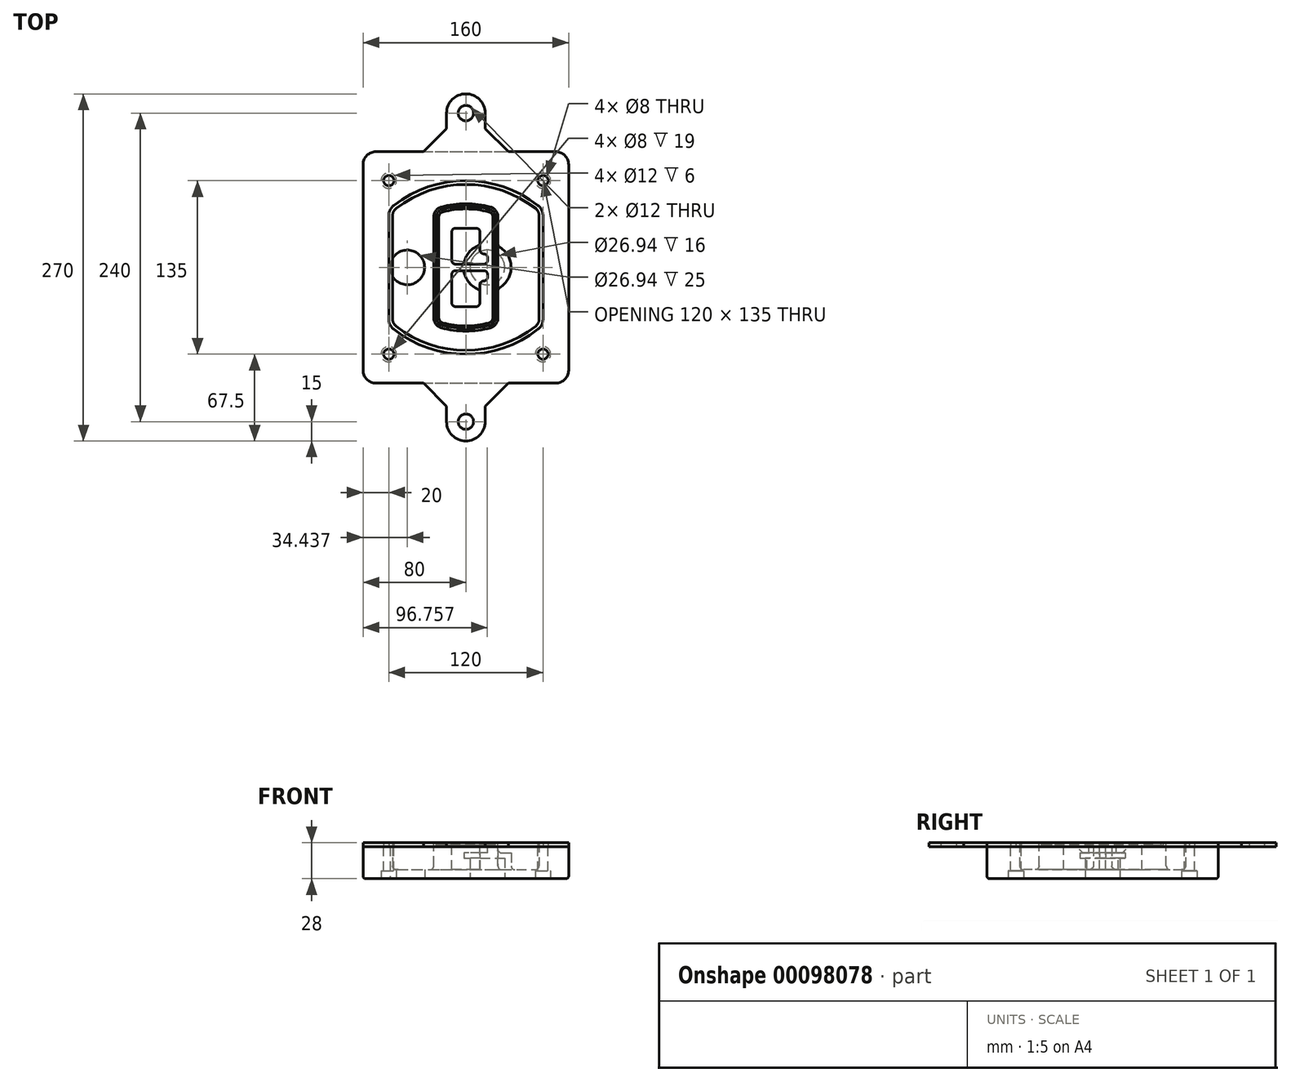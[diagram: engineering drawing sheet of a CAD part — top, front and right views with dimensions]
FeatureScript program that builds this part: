
annotation { "Feature Type Name" : "Feature", "Feature Type Description" : "" }
export const myFeature = defineFeature(function(context is Context, id is Id, definition is map)
    precondition{}
    {
        {
            var Q0;
            Q0=qCreatedBy(makeId("Top.planeOp"),FACE);
            var sketch = newSketch(context, id + "F0", { "sketchPlane" : qUnion([Q0])});
            skPoint(sketch, "E0.rect.middle", {"position": v(0, 0) * mm});
            skLineSegment(sketch, "E1.bottom", {"start": v(-70, -90) * mm, "end": v(70, -90) * mm});
            skLineSegment(sketch, "E1.top", {"start": v(-70, 90) * mm, "end": v(70, 90) * mm});
            skLineSegment(sketch, "E1.left", {"start": v(-80, -80) * mm, "end": v(-80, 80) * mm});
            skLineSegment(sketch, "E1.right", {"start": v(80, -80) * mm, "end": v(80, 80) * mm});
            skLineSegment(sketch, "E2", {"start": v(-80, 90) * mm, "end": v(80, -90) * mm, "construction": true});
            skLineSegment(sketch, "E3", {"start": v(80, 90) * mm, "end": v(-80, -90) * mm, "construction": true});
            skCircle(sketch, "E4", {"center": v(-60, 67.5) * mm, "radius": 4 * mm});
            skCircle(sketch, "E5", {"center": v(60, 67.5) * mm, "radius": 4 * mm});
            skCircle(sketch, "E6", {"center": v(60, -67.5) * mm, "radius": 4 * mm});
            skCircle(sketch, "E7", {"center": v(-60, -67.5) * mm, "radius": 4 * mm});
            skLineSegment(sketch, "E8", {"start": v(-60, 67.5) * mm, "end": v(60, 67.5) * mm, "construction": true});
            skLineSegment(sketch, "E9", {"start": v(60, 67.5) * mm, "end": v(60, -67.5) * mm, "construction": true});
            skLineSegment(sketch, "E10", {"start": v(60, -67.5) * mm, "end": v(-60, -67.5) * mm, "construction": true});
            skLineSegment(sketch, "E11", {"start": v(-60, -67.5) * mm, "end": v(-60, 67.5) * mm, "construction": true});
            skLineSegment(sketch, "E12", {"start": v(-60, 40.3) * mm, "end": v(-60, -40.3) * mm});
            skLineSegment(sketch, "E13", {"start": v(60, 40.3) * mm, "end": v(60, -40.3) * mm});
            skArc(sketch, "E14", {"start": v(56.15, 48.18) * mm, "mid": v(0, 67.5) * mm, "end": v(-56.15, 48.18) * mm});
            skArc(sketch, "E15", {"start": v(-56.15, -48.18) * mm, "mid": v(0, -67.5) * mm, "end": v(56.15, -48.18) * mm});
            skLineSegment(sketch, "E16", {"start": v(-60, 0) * mm, "end": v(60, 0) * mm, "construction": true});
            skPoint(sketch, "E17.visualSharp", {"position": v(-60, -45) * mm});
            skArc(sketch, "E17.filletArc", {"start": v(-60, -40.3) * mm, "mid": v(-58.99, -44.68) * mm, "end": v(-56.15, -48.18) * mm});
            skPoint(sketch, "E18.visualSharp", {"position": v(-60, 45) * mm});
            skArc(sketch, "E18.filletArc", {"start": v(-56.15, 48.18) * mm, "mid": v(-58.99, 44.68) * mm, "end": v(-60, 40.3) * mm});
            skPoint(sketch, "E19.visualSharp", {"position": v(60, 45) * mm});
            skArc(sketch, "E19.filletArc", {"start": v(60, 40.3) * mm, "mid": v(58.99, 44.68) * mm, "end": v(56.15, 48.18) * mm});
            skPoint(sketch, "E20.visualSharp", {"position": v(60, -45) * mm});
            skArc(sketch, "E20.filletArc", {"start": v(56.15, -48.18) * mm, "mid": v(58.99, -44.68) * mm, "end": v(60, -40.3) * mm});
            skPoint(sketch, "E21.visualSharp", {"position": v(-80, 90) * mm});
            skArc(sketch, "E21.filletArc", {"start": v(-70, 90) * mm, "mid": v(-77.07, 87.07) * mm, "end": v(-80, 80) * mm});
            skPoint(sketch, "E22.visualSharp", {"position": v(80, 90) * mm});
            skArc(sketch, "E22.filletArc", {"start": v(80, 80) * mm, "mid": v(77.07, 87.07) * mm, "end": v(70, 90) * mm});
            skPoint(sketch, "E23.visualSharp", {"position": v(80, -90) * mm});
            skArc(sketch, "E23.filletArc", {"start": v(70, -90) * mm, "mid": v(77.07, -87.07) * mm, "end": v(80, -80) * mm});
            skPoint(sketch, "E24.visualSharp", {"position": v(-80, -90) * mm});
            skArc(sketch, "E24.filletArc", {"start": v(-80, -80) * mm, "mid": v(-77.07, -87.07) * mm, "end": v(-70, -90) * mm});
            skArc(sketch, "E25.0", {"start": v(57, 40.3) * mm, "mid": v(56.3, 43.36) * mm, "end": v(54.3, 45.81) * mm});
            skLineSegment(sketch, "E25.1", {"start": v(57, 40.3) * mm, "end": v(57, -40.3) * mm});
            skArc(sketch, "E25.2", {"start": v(54.3, -45.81) * mm, "mid": v(56.3, -43.36) * mm, "end": v(57, -40.3) * mm});
            skArc(sketch, "E25.3", {"start": v(-54.3, -45.81) * mm, "mid": v(0, -64.5) * mm, "end": v(54.3, -45.81) * mm});
            skArc(sketch, "E25.4", {"start": v(-57, -40.3) * mm, "mid": v(-56.3, -43.36) * mm, "end": v(-54.3, -45.81) * mm});
            skArc(sketch, "E25.5", {"start": v(54.3, 45.81) * mm, "mid": v(0, 64.5) * mm, "end": v(-54.3, 45.81) * mm});
            skLineSegment(sketch, "E25.6", {"start": v(-57, 40.3) * mm, "end": v(-57, -40.3) * mm});
            skArc(sketch, "E25.7", {"start": v(-54.3, 45.81) * mm, "mid": v(-56.3, 43.36) * mm, "end": v(-57, 40.3) * mm});
            skArc(sketch, "E26.0", {"start": v(-58.62, 51.33) * mm, "mid": v(-62.58, 46.43) * mm, "end": v(-64, 40.3) * mm});
            skArc(sketch, "E26.1", {"start": v(58.62, 51.33) * mm, "mid": v(0, 71.5) * mm, "end": v(-58.62, 51.33) * mm});
            skArc(sketch, "E26.2", {"start": v(64, 40.3) * mm, "mid": v(62.58, 46.43) * mm, "end": v(58.62, 51.33) * mm});
            skLineSegment(sketch, "E26.3", {"start": v(64, 40.3) * mm, "end": v(64, -40.3) * mm});
            skArc(sketch, "E26.4", {"start": v(58.62, -51.33) * mm, "mid": v(62.58, -46.43) * mm, "end": v(64, -40.3) * mm});
            skLineSegment(sketch, "E26.5", {"start": v(-64, 40.3) * mm, "end": v(-64, -40.3) * mm});
            skArc(sketch, "E26.6", {"start": v(-58.62, -51.33) * mm, "mid": v(0, -71.5) * mm, "end": v(58.62, -51.33) * mm});
            skArc(sketch, "E26.7", {"start": v(-64, -40.3) * mm, "mid": v(-62.58, -46.43) * mm, "end": v(-58.62, -51.33) * mm});
            skSolve(sketch);
        }
        {
            var Q0;
            Q0=makeQuery(id+"F0.imprint","IMPRINT",FACE,{"disambiguationData":[TD([[makeQuery(id+"F0.imprint","IMPRINT",EDGE,{"derivedFrom":sQuery(id+"F0.wireOp",EDGE,"E1.bottom")}),1.0]])]});
            var Q1;
            Q1=makeQuery(id+"F0.imprint","IMPRINT",FACE,{"disambiguationData":[TD([[makeQuery(id+"F0.imprint","IMPRINT",EDGE,{"derivedFrom":sQuery(id+"F0.wireOp",EDGE,"E12")}),1.0]])]});
            var Q2;
            Q2=makeQuery(id+"F0.imprint","IMPRINT",FACE,{"disambiguationData":[TD([[makeQuery(id+"F0.imprint","IMPRINT",EDGE,{"derivedFrom":sQuery(id+"F0.wireOp",EDGE,"E25.0")}),1.0]])]});
            var Q3;
            Q3=makeQuery(id+"F0.imprint","IMPRINT",FACE,{"disambiguationData":[TD([[makeQuery(id+"F0.imprint","IMPRINT",EDGE,{"derivedFrom":sQuery(id+"F0.wireOp",EDGE,"E12")}),-1.0]])]});
            extrude(context, id + "F1", {"entities" : qUnion([Q0, Q1, Q2, Q3]), "oppositeDirection" : true, "depth" : 25 * mm});
        }
        {
            var Q0;
            Q0=makeQuery(id+"F0.imprint","IMPRINT",FACE,{"disambiguationData":[TD([[makeQuery(id+"F0.imprint","IMPRINT",EDGE,{"derivedFrom":sQuery(id+"F0.wireOp",EDGE,"E12")}),1.0]])]});
            extrude(context, id + "F2", {"entities" : qUnion([Q0]), "operationType" : NewBodyOperationType.ADD, "depth" : 3 * mm});
        }
        {
            var Q0;
            Q0=makeQuery(id+"F0.imprint","IMPRINT",FACE,{"disambiguationData":[TD([[makeQuery(id+"F0.imprint","IMPRINT",EDGE,{"derivedFrom":sQuery(id+"F0.wireOp",EDGE,"E25.0")}),1.0]])]});
            extrude(context, id + "F3", {"entities" : qUnion([Q0]), "operationType" : NewBodyOperationType.REMOVE, "oppositeDirection" : true, "depth" : 18 * mm});
        }
        {
            var Q0;
            Q0=makeQuery(id+"F2.opExtrude","CAP_FACE",FACE,{"disambiguationData":[OSD([sQuery(id+"F0.wireOp",EDGE,"E12"),sQuery(id+"F0.wireOp",EDGE,"E13"),sQuery(id+"F0.wireOp",EDGE,"E14"),sQuery(id+"F0.wireOp",EDGE,"E15"),sQuery(id+"F0.wireOp",EDGE,"E17.filletArc"),sQuery(id+"F0.wireOp",EDGE,"E18.filletArc"),sQuery(id+"F0.wireOp",EDGE,"E19.filletArc"),sQuery(id+"F0.wireOp",EDGE,"E20.filletArc"),sQuery(id+"F0.wireOp",EDGE,"E25.0"),sQuery(id+"F0.wireOp",EDGE,"E25.1"),sQuery(id+"F0.wireOp",EDGE,"E25.2"),sQuery(id+"F0.wireOp",EDGE,"E25.3"),sQuery(id+"F0.wireOp",EDGE,"E25.4"),sQuery(id+"F0.wireOp",EDGE,"E25.5"),sQuery(id+"F0.wireOp",EDGE,"E25.6"),sQuery(id+"F0.wireOp",EDGE,"E25.7")])],"isStart":false});
            var sketch = newSketch(context, id + "F4", { "sketchPlane" : qUnion([Q0])});
            skArc(sketch, "E27.0", {"start": v(-19.08, -46.97) * mm, "mid": v(0, -49.5) * mm, "end": v(19.08, -46.97) * mm});
            skArc(sketch, "E28.0", {"start": v(19.08, 46.97) * mm, "mid": v(0, 49.5) * mm, "end": v(-19.08, 46.97) * mm});
            skLineSegment(sketch, "E29", {"start": v(-25, 39.25) * mm, "end": v(-25, -39.25) * mm});
            skLineSegment(sketch, "E30", {"start": v(25, 39.25) * mm, "end": v(25, -39.25) * mm});
            skLineSegment(sketch, "E31", {"start": v(-25, 45.1) * mm, "end": v(25, 45.1) * mm, "construction": true});
            skLineSegment(sketch, "E32", {"start": v(-25, -45.1) * mm, "end": v(25, -45.1) * mm, "construction": true});
            skPoint(sketch, "E33.visualSharp", {"position": v(-25, 45.1) * mm});
            skArc(sketch, "E33.filletArc", {"start": v(-19.08, 46.97) * mm, "mid": v(-23.35, 44.11) * mm, "end": v(-25, 39.25) * mm});
            skPoint(sketch, "E34.visualSharp", {"position": v(25, 45.1) * mm});
            skArc(sketch, "E34.filletArc", {"start": v(25, 39.25) * mm, "mid": v(23.35, 44.11) * mm, "end": v(19.08, 46.97) * mm});
            skPoint(sketch, "E35.visualSharp", {"position": v(25, -45.1) * mm});
            skArc(sketch, "E35.filletArc", {"start": v(19.08, -46.97) * mm, "mid": v(23.35, -44.11) * mm, "end": v(25, -39.25) * mm});
            skPoint(sketch, "E36.visualSharp", {"position": v(-25, -45.1) * mm});
            skArc(sketch, "E36.filletArc", {"start": v(-25, -39.25) * mm, "mid": v(-23.35, -44.11) * mm, "end": v(-19.08, -46.97) * mm});
            skArc(sketch, "E37.0", {"start": v(54.3, 45.81) * mm, "mid": v(0, 64.5) * mm, "end": v(-54.3, 45.81) * mm});
            skArc(sketch, "E37.1", {"start": v(-54.3, 45.81) * mm, "mid": v(-56.3, 43.36) * mm, "end": v(-57, 40.3) * mm});
            skLineSegment(sketch, "E37.2", {"start": v(-57, 40.3) * mm, "end": v(-57, -40.3) * mm});
            skArc(sketch, "E37.3", {"start": v(-57, -40.3) * mm, "mid": v(-56.3, -43.36) * mm, "end": v(-54.3, -45.81) * mm});
            skArc(sketch, "E37.4", {"start": v(-54.3, -45.81) * mm, "mid": v(0, -64.5) * mm, "end": v(54.3, -45.81) * mm});
            skArc(sketch, "E37.5", {"start": v(54.3, -45.81) * mm, "mid": v(56.3, -43.36) * mm, "end": v(57, -40.3) * mm});
            skLineSegment(sketch, "E37.6", {"start": v(57, 40.3) * mm, "end": v(57, -40.3) * mm});
            skArc(sketch, "E37.7", {"start": v(57, 40.3) * mm, "mid": v(56.3, 43.36) * mm, "end": v(54.3, 45.81) * mm});
            skLineSegment(sketch, "E38.0", {"start": v(23, 39.25) * mm, "end": v(23, -39.25) * mm});
            skArc(sketch, "E38.1", {"start": v(18.56, -45.04) * mm, "mid": v(21.76, -42.9) * mm, "end": v(23, -39.25) * mm});
            skArc(sketch, "E38.2", {"start": v(-18.56, -45.04) * mm, "mid": v(0, -47.5) * mm, "end": v(18.56, -45.04) * mm});
            skArc(sketch, "E38.3", {"start": v(-23, -39.25) * mm, "mid": v(-21.76, -42.9) * mm, "end": v(-18.56, -45.04) * mm});
            skLineSegment(sketch, "E38.4", {"start": v(-23, 39.25) * mm, "end": v(-23, -39.25) * mm});
            skArc(sketch, "E38.5", {"start": v(23, 39.25) * mm, "mid": v(21.76, 42.9) * mm, "end": v(18.56, 45.04) * mm});
            skArc(sketch, "E38.6", {"start": v(-18.56, 45.04) * mm, "mid": v(-21.76, 42.9) * mm, "end": v(-23, 39.25) * mm});
            skArc(sketch, "E38.7", {"start": v(18.56, 45.04) * mm, "mid": v(0, 47.5) * mm, "end": v(-18.56, 45.04) * mm});
            skArc(sketch, "E39.0", {"start": v(21, 39.25) * mm, "mid": v(20.18, 41.68) * mm, "end": v(18.04, 43.1) * mm});
            skLineSegment(sketch, "E39.1", {"start": v(21, 39.25) * mm, "end": v(21, -39.25) * mm});
            skArc(sketch, "E39.2", {"start": v(18.04, -43.1) * mm, "mid": v(20.18, -41.68) * mm, "end": v(21, -39.25) * mm});
            skArc(sketch, "E39.3", {"start": v(-18.04, -43.1) * mm, "mid": v(0, -45.5) * mm, "end": v(18.04, -43.1) * mm});
            skArc(sketch, "E39.4", {"start": v(-21, -39.25) * mm, "mid": v(-20.18, -41.68) * mm, "end": v(-18.04, -43.1) * mm});
            skArc(sketch, "E39.5", {"start": v(18.04, 43.1) * mm, "mid": v(0, 45.5) * mm, "end": v(-18.04, 43.1) * mm});
            skLineSegment(sketch, "E39.6", {"start": v(-21, 39.25) * mm, "end": v(-21, -39.25) * mm});
            skArc(sketch, "E39.7", {"start": v(-18.04, 43.1) * mm, "mid": v(-20.18, 41.68) * mm, "end": v(-21, 39.25) * mm});
            skLineSegment(sketch, "E40", {"start": v(-25, 0) * mm, "end": v(25, 0) * mm, "construction": true});
            skLineSegment(sketch, "E41", {"start": v(-11, 5.5) * mm, "end": v(-11, 27.5) * mm});
            skLineSegment(sketch, "E42", {"start": v(-8, 30.5) * mm, "end": v(8, 30.5) * mm});
            skLineSegment(sketch, "E43", {"start": v(11, 27.5) * mm, "end": v(11, 13.5) * mm});
            skLineSegment(sketch, "E44", {"start": v(14, 10.5) * mm, "end": v(14, 10.5) * mm});
            skLineSegment(sketch, "E45", {"start": v(17, 7.5) * mm, "end": v(17, 5.5) * mm});
            skLineSegment(sketch, "E46", {"start": v(14, 2.5) * mm, "end": v(-8, 2.5) * mm});
            skPoint(sketch, "E47.visualSharp", {"position": v(-11, 30.5) * mm});
            skArc(sketch, "E47.filletArc", {"start": v(-8, 30.5) * mm, "mid": v(-10.12, 29.62) * mm, "end": v(-11, 27.5) * mm});
            skPoint(sketch, "E48.visualSharp", {"position": v(11, 30.5) * mm});
            skArc(sketch, "E48.filletArc", {"start": v(11, 27.5) * mm, "mid": v(10.12, 29.62) * mm, "end": v(8, 30.5) * mm});
            skPoint(sketch, "E49.visualSharp", {"position": v(11, 10.5) * mm});
            skArc(sketch, "E49.filletArc", {"start": v(11, 13.5) * mm, "mid": v(11.88, 11.38) * mm, "end": v(14, 10.5) * mm});
            skPoint(sketch, "E50.visualSharp", {"position": v(17, 10.5) * mm});
            skArc(sketch, "E50.filletArc", {"start": v(17, 7.5) * mm, "mid": v(16.12, 9.62) * mm, "end": v(14, 10.5) * mm});
            skPoint(sketch, "E51.visualSharp", {"position": v(17, 2.5) * mm});
            skArc(sketch, "E51.filletArc", {"start": v(14, 2.5) * mm, "mid": v(16.12, 3.38) * mm, "end": v(17, 5.5) * mm});
            skPoint(sketch, "E52.visualSharp", {"position": v(-11, 2.5) * mm});
            skArc(sketch, "E52.filletArc", {"start": v(-11, 5.5) * mm, "mid": v(-10.12, 3.38) * mm, "end": v(-8, 2.5) * mm});
            skLineSegment(sketch, "E53.0.MirrorCS", {"start": v(14, -2.5) * mm, "end": v(-8, -2.5) * mm});
            skArc(sketch, "E54.0.MirrorCS", {"start": v(-11, -5.5) * mm, "mid": v(-10.12, -3.38) * mm, "end": v(-8, -2.5) * mm});
            skLineSegment(sketch, "E55.0.MirrorCS", {"start": v(-11, -5.5) * mm, "end": v(-11, -27.5) * mm});
            skArc(sketch, "E56.0.MirrorCS", {"start": v(-8, -30.5) * mm, "mid": v(-10.12, -29.62) * mm, "end": v(-11, -27.5) * mm});
            skLineSegment(sketch, "E57.0.MirrorCS", {"start": v(-8, -30.5) * mm, "end": v(8, -30.5) * mm});
            skArc(sketch, "E58.0.MirrorCS", {"start": v(11, -27.5) * mm, "mid": v(10.12, -29.62) * mm, "end": v(8, -30.5) * mm});
            skLineSegment(sketch, "E59.0.MirrorCS", {"start": v(11, -27.5) * mm, "end": v(11, -13.5) * mm});
            skArc(sketch, "E60.0.MirrorCS", {"start": v(11, -13.5) * mm, "mid": v(11.88, -11.38) * mm, "end": v(14, -10.5) * mm});
            skArc(sketch, "E61.0.MirrorCS", {"start": v(17, -7.5) * mm, "mid": v(16.12, -9.62) * mm, "end": v(14, -10.5) * mm});
            skLineSegment(sketch, "E62.0.MirrorCS", {"start": v(17, -7.5) * mm, "end": v(17, -5.5) * mm});
            skArc(sketch, "E63.0.MirrorCS", {"start": v(14, -2.5) * mm, "mid": v(16.12, -3.38) * mm, "end": v(17, -5.5) * mm});
            skSolve(sketch);
        }
        {
            var Q0;
            Q0=makeQuery(id+"F4.imprint","IMPRINT",FACE,{"disambiguationData":[TD([[makeQuery(id+"F4.imprint","IMPRINT",EDGE,{"derivedFrom":sQuery(id+"F4.wireOp",EDGE,"E27.0")}),1.0]])]});
            var Q1;
            Q1=makeQuery(id+"F4.imprint","IMPRINT",FACE,{"disambiguationData":[TD([[makeQuery(id+"F4.imprint","IMPRINT",EDGE,{"derivedFrom":sQuery(id+"F4.wireOp",EDGE,"E38.0")}),-1.0]])]});
            var Q2;
            Q2=makeQuery(id+"F4.imprint","IMPRINT",FACE,{"disambiguationData":[TD([[makeQuery(id+"F4.imprint","IMPRINT",EDGE,{"derivedFrom":sQuery(id+"F4.wireOp",EDGE,"E39.0")}),1.0]])]});
            extrude(context, id + "F5", {"entities" : qUnion([Q0, Q1, Q2]), "operationType" : NewBodyOperationType.ADD, "endBound" : BoundingType.UP_TO_NEXT, "oppositeDirection" : true, "depth" : 25 * mm});
        }
        {
            var Q0;
            Q0=makeQuery(id+"F4.imprint","IMPRINT",FACE,{"disambiguationData":[TD([[makeQuery(id+"F4.imprint","IMPRINT",EDGE,{"derivedFrom":sQuery(id+"F4.wireOp",EDGE,"E38.0")}),-1.0]])]});
            extrude(context, id + "F6", {"entities" : qUnion([Q0]), "operationType" : NewBodyOperationType.REMOVE, "oppositeDirection" : true, "depth" : 2 * mm});
        }
        {
            var Q0;
            Q0=makeQuery(id+"F1.opExtrude","CAP_FACE",FACE,{"disambiguationData":[OSD([sQuery(id+"F0.wireOp",EDGE,"E1.bottom"),sQuery(id+"F0.wireOp",EDGE,"E1.top"),sQuery(id+"F0.wireOp",EDGE,"E1.left"),sQuery(id+"F0.wireOp",EDGE,"E1.right"),sQuery(id+"F0.wireOp",EDGE,"E4"),sQuery(id+"F0.wireOp",EDGE,"E5"),sQuery(id+"F0.wireOp",EDGE,"E6"),sQuery(id+"F0.wireOp",EDGE,"E7"),sQuery(id+"F0.wireOp",EDGE,"E21.filletArc"),sQuery(id+"F0.wireOp",EDGE,"E22.filletArc"),sQuery(id+"F0.wireOp",EDGE,"E23.filletArc"),sQuery(id+"F0.wireOp",EDGE,"E24.filletArc")])],"isStart":false});
            var sketch = newSketch(context, id + "F7", { "sketchPlane" : qUnion([Q0])});
            skCircle(sketch, "E64", {"center": v(16.76, 0) * mm, "radius": 13.47 * mm});
            skCircle(sketch, "E65", {"center": v(-45.56, 0) * mm, "radius": 13.47 * mm});
            skLineSegment(sketch, "E66", {"start": v(80, 0) * mm, "end": v(-80, 0) * mm});
            skCircle(sketch, "E67", {"center": v(16.76, 0) * mm, "radius": 18.47 * mm});
            skCircle(sketch, "E68", {"center": v(60, -67.5) * mm, "radius": 6 * mm});
            skCircle(sketch, "E69", {"center": v(-60, -67.5) * mm, "radius": 6 * mm});
            skCircle(sketch, "E70", {"center": v(-60, 67.5) * mm, "radius": 6 * mm});
            skCircle(sketch, "E71", {"center": v(60, 67.5) * mm, "radius": 6 * mm});
            skSolve(sketch);
        }
        {
            var Q0;
            {var subQ1=sQuery(id+"F7.wireOp",EDGE,"E66");var subQ4=sQuery(id+"F7.wireOp",EDGE,"E64");var subQ6=makeQuery(id+"F7.imprint","INTERSECT",VERTEX,{"disambiguationData":[OD(0.0)],"derivedFrom":[subQ4,subQ1]});Q0=makeQuery(id+"F7.imprint","IMPRINT",FACE,{"disambiguationData":[TD([[makeQuery(id+"F7.imprint","IMPRINT",EDGE,{"disambiguationData":[TD([[subQ6,-1.0]])],"derivedFrom":subQ4}),-1.0]])]});}
            var Q1;
            {var subQ0=sQuery(id+"F7.wireOp",EDGE,"E66");var subQ1=sQuery(id+"F7.wireOp",EDGE,"E64");var subQ3=makeQuery(id+"F7.imprint","INTERSECT",VERTEX,{"disambiguationData":[OD(0.0)],"derivedFrom":[subQ1,subQ0]});Q1=makeQuery(id+"F7.imprint","IMPRINT",FACE,{"disambiguationData":[TD([[makeQuery(id+"F7.imprint","IMPRINT",EDGE,{"disambiguationData":[TD([[subQ3,-1.0]])],"derivedFrom":subQ1}),1.0]])]});}
            var Q2;
            {var subQ0=sQuery(id+"F7.wireOp",EDGE,"E66");var subQ1=sQuery(id+"F7.wireOp",EDGE,"E64");var subQ3=makeQuery(id+"F7.imprint","INTERSECT",VERTEX,{"disambiguationData":[OD(0.0)],"derivedFrom":[subQ1,subQ0]});Q2=makeQuery(id+"F7.imprint","IMPRINT",FACE,{"disambiguationData":[TD([[makeQuery(id+"F7.imprint","IMPRINT",EDGE,{"disambiguationData":[TD([[subQ3,1.0]])],"derivedFrom":subQ1}),1.0]])]});}
            var Q3;
            {var subQ1=sQuery(id+"F7.wireOp",EDGE,"E66");var subQ4=sQuery(id+"F7.wireOp",EDGE,"E64");var subQ6=makeQuery(id+"F7.imprint","INTERSECT",VERTEX,{"disambiguationData":[OD(0.0)],"derivedFrom":[subQ4,subQ1]});Q3=makeQuery(id+"F7.imprint","IMPRINT",FACE,{"disambiguationData":[TD([[makeQuery(id+"F7.imprint","IMPRINT",EDGE,{"disambiguationData":[TD([[subQ6,1.0]])],"derivedFrom":subQ4}),-1.0]])]});}
            extrude(context, id + "F8", {"entities" : qUnion([Q0, Q1, Q2, Q3]), "operationType" : NewBodyOperationType.ADD, "oppositeDirection" : true, "depth" : 20 * mm});
        }
        {
            var Q0;
            {var subQ0=sQuery(id+"F7.wireOp",EDGE,"E66");var subQ1=sQuery(id+"F7.wireOp",EDGE,"E64");var subQ3=makeQuery(id+"F7.imprint","INTERSECT",VERTEX,{"disambiguationData":[OD(0.0)],"derivedFrom":[subQ1,subQ0]});Q0=makeQuery(id+"F7.imprint","IMPRINT",FACE,{"disambiguationData":[TD([[makeQuery(id+"F7.imprint","IMPRINT",EDGE,{"disambiguationData":[TD([[subQ3,-1.0]])],"derivedFrom":subQ1}),1.0]])]});}
            var Q1;
            {var subQ0=sQuery(id+"F7.wireOp",EDGE,"E66");var subQ1=sQuery(id+"F7.wireOp",EDGE,"E64");var subQ3=makeQuery(id+"F7.imprint","INTERSECT",VERTEX,{"disambiguationData":[OD(0.0)],"derivedFrom":[subQ1,subQ0]});Q1=makeQuery(id+"F7.imprint","IMPRINT",FACE,{"disambiguationData":[TD([[makeQuery(id+"F7.imprint","IMPRINT",EDGE,{"disambiguationData":[TD([[subQ3,1.0]])],"derivedFrom":subQ1}),1.0]])]});}
            extrude(context, id + "F9", {"entities" : qUnion([Q0, Q1]), "operationType" : NewBodyOperationType.REMOVE, "oppositeDirection" : true, "depth" : 16 * mm});
        }
        {
            var Q0;
            {var subQ0=sQuery(id+"F7.wireOp",EDGE,"E66");var subQ1=sQuery(id+"F7.wireOp",EDGE,"E65");var subQ3=makeQuery(id+"F7.imprint","INTERSECT",VERTEX,{"disambiguationData":[OD(0.0)],"derivedFrom":[subQ1,subQ0]});Q0=makeQuery(id+"F7.imprint","IMPRINT",FACE,{"disambiguationData":[TD([[makeQuery(id+"F7.imprint","IMPRINT",EDGE,{"disambiguationData":[TD([[subQ3,-1.0]])],"derivedFrom":subQ1}),1.0]])]});}
            var Q1;
            {var subQ0=sQuery(id+"F7.wireOp",EDGE,"E66");var subQ1=sQuery(id+"F7.wireOp",EDGE,"E65");var subQ3=makeQuery(id+"F7.imprint","INTERSECT",VERTEX,{"disambiguationData":[OD(0.0)],"derivedFrom":[subQ1,subQ0]});Q1=makeQuery(id+"F7.imprint","IMPRINT",FACE,{"disambiguationData":[TD([[makeQuery(id+"F7.imprint","IMPRINT",EDGE,{"disambiguationData":[TD([[subQ3,1.0]])],"derivedFrom":subQ1}),1.0]])]});}
            extrude(context, id + "F10", {"entities" : qUnion([Q0, Q1]), "operationType" : NewBodyOperationType.REMOVE, "oppositeDirection" : true, "depth" : 25 * mm});
        }
        {
            var Q0;
            Q0=makeQuery(id+"F7.imprint","IMPRINT",FACE,{"disambiguationData":[TD([[makeQuery(id+"F7.imprint","IMPRINT",EDGE,{"derivedFrom":sQuery(id+"F7.wireOp",EDGE,"E68")}),1.0]])]});
            var Q1;
            Q1=makeQuery(id+"F7.imprint","IMPRINT",FACE,{"disambiguationData":[TD([[makeQuery(id+"F7.imprint","IMPRINT",EDGE,{"derivedFrom":makeQuery(id+"F1.opExtrude","CAP_EDGE",EDGE,{"disambiguationData":[OSD([sQuery(id+"F0.wireOp",EDGE,"E5")])],"isStart":false})}),-1.0]])]});
            var Q2;
            Q2=makeQuery(id+"F7.imprint","IMPRINT",FACE,{"disambiguationData":[TD([[makeQuery(id+"F7.imprint","IMPRINT",EDGE,{"derivedFrom":sQuery(id+"F7.wireOp",EDGE,"E69")}),1.0]])]});
            var Q3;
            Q3=makeQuery(id+"F7.imprint","IMPRINT",FACE,{"disambiguationData":[TD([[makeQuery(id+"F7.imprint","IMPRINT",EDGE,{"derivedFrom":makeQuery(id+"F1.opExtrude","CAP_EDGE",EDGE,{"disambiguationData":[OSD([sQuery(id+"F0.wireOp",EDGE,"E4")])],"isStart":false})}),-1.0]])]});
            var Q4;
            Q4=makeQuery(id+"F7.imprint","IMPRINT",FACE,{"disambiguationData":[TD([[makeQuery(id+"F7.imprint","IMPRINT",EDGE,{"derivedFrom":sQuery(id+"F7.wireOp",EDGE,"E70")}),1.0]])]});
            var Q5;
            Q5=makeQuery(id+"F7.imprint","IMPRINT",FACE,{"disambiguationData":[TD([[makeQuery(id+"F7.imprint","IMPRINT",EDGE,{"derivedFrom":makeQuery(id+"F1.opExtrude","CAP_EDGE",EDGE,{"disambiguationData":[OSD([sQuery(id+"F0.wireOp",EDGE,"E7")])],"isStart":false})}),-1.0]])]});
            var Q6;
            Q6=makeQuery(id+"F7.imprint","IMPRINT",FACE,{"disambiguationData":[TD([[makeQuery(id+"F7.imprint","IMPRINT",EDGE,{"derivedFrom":sQuery(id+"F7.wireOp",EDGE,"E71")}),1.0]])]});
            var Q7;
            Q7=makeQuery(id+"F7.imprint","IMPRINT",FACE,{"disambiguationData":[TD([[makeQuery(id+"F7.imprint","IMPRINT",EDGE,{"derivedFrom":makeQuery(id+"F1.opExtrude","CAP_EDGE",EDGE,{"disambiguationData":[OSD([sQuery(id+"F0.wireOp",EDGE,"E6")])],"isStart":false})}),-1.0]])]});
            extrude(context, id + "F11", {"entities" : qUnion([Q0, Q1, Q2, Q3, Q4, Q5, Q6, Q7]), "operationType" : NewBodyOperationType.REMOVE, "oppositeDirection" : true, "depth" : 6 * mm});
        }
        {
            var Q0;
            Q0=makeQuery(id+"F9.boolean.opBoolean","COPY",FACE,{"derivedFrom":makeQuery(id+"F9.opExtrude","CAP_FACE",FACE,{"disambiguationData":[OSD([sQuery(id+"F7.wireOp",EDGE,"E64")])],"isStart":false})});
            var sketch = newSketch(context, id + "F12", { "sketchPlane" : qUnion([Q0])});
            skArc(sketch, "E72.0", {"start": v(11, 17.55) * mm, "mid": v(2.57, 11.82) * mm, "end": v(-1.54, 2.5) * mm});
            skArc(sketch, "E72.1", {"start": v(-1.54, -2.5) * mm, "mid": v(2.57, -11.82) * mm, "end": v(11, -17.55) * mm});
            skLineSegment(sketch, "E73", {"start": v(-1.54, -2.5) * mm, "end": v(14, -2.5) * mm});
            skLineSegment(sketch, "E74.0", {"start": v(14, 2.5) * mm, "end": v(-1.54, 2.5) * mm});
            skArc(sketch, "E74.1", {"start": v(14, 2.5) * mm, "mid": v(16.12, 3.38) * mm, "end": v(17, 5.5) * mm});
            skLineSegment(sketch, "E74.2", {"start": v(17, 7.5) * mm, "end": v(17, 5.5) * mm});
            skArc(sketch, "E74.3", {"start": v(17, 7.5) * mm, "mid": v(16.12, 9.62) * mm, "end": v(14, 10.5) * mm});
            skArc(sketch, "E74.4", {"start": v(11, 13.5) * mm, "mid": v(11.88, 11.38) * mm, "end": v(14, 10.5) * mm});
            skLineSegment(sketch, "E74.5", {"start": v(11, 17.55) * mm, "end": v(11, 13.5) * mm});
            skLineSegment(sketch, "E74.7", {"start": v(14, -2.5) * mm, "end": v(-1.54, -2.5) * mm});
            skArc(sketch, "E74.8", {"start": v(14, -2.5) * mm, "mid": v(16.12, -3.38) * mm, "end": v(17, -5.5) * mm});
            skLineSegment(sketch, "E74.9", {"start": v(17, -7.5) * mm, "end": v(17, -5.5) * mm});
            skArc(sketch, "E74.10", {"start": v(17, -7.5) * mm, "mid": v(16.12, -9.62) * mm, "end": v(14, -10.5) * mm});
            skArc(sketch, "E74.11", {"start": v(11, -13.5) * mm, "mid": v(11.88, -11.38) * mm, "end": v(14, -10.5) * mm});
            skLineSegment(sketch, "E74.12", {"start": v(11, -17.55) * mm, "end": v(11, -13.5) * mm});
            skPoint(sketch, "E75.orphan", {"position": v(11, -27.5) * mm});
            skPoint(sketch, "E76.orphan", {"position": v(-8, -2.5) * mm});
            skPoint(sketch, "E77.orphan", {"position": v(-8, 2.5) * mm});
            skPoint(sketch, "E78.orphan", {"position": v(11, 27.5) * mm});
            skSolve(sketch);
        }
        {
            var Q0;
            {var subQ7=sQuery(id+"F12.wireOp",EDGE,"E72.0");var subQ14=sQuery(id+"F12.wireOp",EDGE,"E72.1");var subQ16=sQuery(id+"F12.wireOp",EDGE,"E74.1");var subQ18=sQuery(id+"F12.wireOp",EDGE,"E74.8");Q0=qUnion([makeQuery(id+"F12.imprint","IMPRINT",FACE,{"disambiguationData":[TD([[makeQuery(id+"F12.imprint","IMPRINT",EDGE,{"derivedFrom":subQ7}),1.0]])]}),makeQuery(id+"F12.imprint","IMPRINT",FACE,{"disambiguationData":[TD([[makeQuery(id+"F12.imprint","IMPRINT",EDGE,{"derivedFrom":subQ14}),1.0]])]}),makeQuery(id+"F12.imprint","IMPRINT",FACE,{"disambiguationData":[TD([[makeQuery(id+"F12.imprint","IMPRINT",EDGE,{"derivedFrom":subQ16}),1.0]])]}),makeQuery(id+"F12.imprint","IMPRINT",FACE,{"disambiguationData":[TD([[makeQuery(id+"F12.imprint","IMPRINT",EDGE,{"derivedFrom":subQ18}),-1.0]])]})]);}
            var Q1;
            Q1=makeQuery(id+"F5.boolean.opBoolean","SPLIT",FACE,{"disambiguationData":[TD([makeQuery(id+"F5.opExtrude","SWEPT_FACE",FACE,{"disambiguationData":[OSD([sQuery(id+"F4.wireOp",EDGE,"E41")])]})])],"derivedFrom":makeQuery(id+"F3.boolean.opBoolean","COPY",FACE,{"derivedFrom":makeQuery(id+"F3.opExtrude","CAP_FACE",FACE,{"disambiguationData":[OSD([sQuery(id+"F0.wireOp",EDGE,"E25.0"),sQuery(id+"F0.wireOp",EDGE,"E25.1"),sQuery(id+"F0.wireOp",EDGE,"E25.2"),sQuery(id+"F0.wireOp",EDGE,"E25.3"),sQuery(id+"F0.wireOp",EDGE,"E25.4"),sQuery(id+"F0.wireOp",EDGE,"E25.5"),sQuery(id+"F0.wireOp",EDGE,"E25.6"),sQuery(id+"F0.wireOp",EDGE,"E25.7")])],"isStart":false})})});
            extrude(context, id + "F13", {"entities" : qUnion([Q0]), "operationType" : NewBodyOperationType.REMOVE, "endBound" : BoundingType.UP_TO_SURFACE, "endBoundEntityFace" : qUnion([Q1]), "depth" : 25 * mm});
        }
        {
            var Q0;
            Q0=makeQuery(id+"F3.boolean.opBoolean","COPY",EDGE,{"derivedFrom":makeQuery(id+"F3.opExtrude","CAP_EDGE",EDGE,{"disambiguationData":[OSD([sQuery(id+"F0.wireOp",EDGE,"E25.6")])],"isStart":false})});
            var Q1;
            Q1=makeQuery(id+"F8.boolean.opBoolean","INTERSECT",EDGE,{"derivedFrom":[makeQuery(id+"F5.opExtrude","SWEPT_FACE",FACE,{"disambiguationData":[OSD([sQuery(id+"F4.wireOp",EDGE,"E30")])]}),makeQuery(id+"F8.opExtrude","CAP_FACE",FACE,{"disambiguationData":[OSD([sQuery(id+"F7.wireOp",EDGE,"E67")])],"isStart":false})]});
            var Q2;
            Q2=makeQuery(id+"F8.boolean.opBoolean","INTERSECT",EDGE,{"disambiguationData":[OD(1.0)],"derivedFrom":[makeQuery(id+"F5.opExtrude","SWEPT_FACE",FACE,{"disambiguationData":[OSD([sQuery(id+"F4.wireOp",EDGE,"E30")])]}),makeQuery(id+"F8.opExtrude","SWEPT_FACE",FACE,{"disambiguationData":[OSD([sQuery(id+"F7.wireOp",EDGE,"E67")])]})]});
            var Q3;
            {var subQ0=sQuery(id+"F4.wireOp",EDGE,"E30");Q3=makeQuery(id+"F8.boolean.opBoolean","SPLIT",EDGE,{"disambiguationData":[TD([makeQuery(id+"F5.opExtrude","SWEPT_FACE",FACE,{"disambiguationData":[OSD([sQuery(id+"F4.wireOp",EDGE,"E35.filletArc")])]})])],"derivedFrom":makeQuery(id+"F5.opExtrude","CAP_EDGE",EDGE,{"disambiguationData":[OSD([subQ0])],"isStart":false})});}
            var Q4;
            {var subQ0=sQuery(id+"F0.wireOp",EDGE,"E25.7");var subQ1=sQuery(id+"F0.wireOp",EDGE,"E25.1");var subQ2=sQuery(id+"F0.wireOp",EDGE,"E25.6");var subQ3=sQuery(id+"F0.wireOp",EDGE,"E25.5");var subQ4=sQuery(id+"F0.wireOp",EDGE,"E25.4");var subQ5=sQuery(id+"F0.wireOp",EDGE,"E25.0");var subQ6=sQuery(id+"F0.wireOp",EDGE,"E25.2");var subQ7=sQuery(id+"F0.wireOp",EDGE,"E25.3");Q4=makeQuery(id+"F8.boolean.opBoolean","INTERSECT",EDGE,{"derivedFrom":[makeQuery(id+"F5.boolean.opBoolean","SPLIT",FACE,{"disambiguationData":[TD([makeQuery(id+"F2.opExtrude","SWEPT_FACE",FACE,{"disambiguationData":[OSD([subQ5])]})])],"derivedFrom":makeQuery(id+"F3.boolean.opBoolean","COPY",FACE,{"derivedFrom":makeQuery(id+"F3.opExtrude","CAP_FACE",FACE,{"disambiguationData":[OSD([subQ5,subQ1,subQ6,subQ7,subQ4,subQ3,subQ2,subQ0])],"isStart":false})})}),makeQuery(id+"F8.opExtrude","SWEPT_FACE",FACE,{"disambiguationData":[OSD([sQuery(id+"F7.wireOp",EDGE,"E67")])]})]});}
            var Q5;
            Q5=makeQuery(id+"F8.boolean.opBoolean","INTERSECT",EDGE,{"disambiguationData":[OD(0.0)],"derivedFrom":[makeQuery(id+"F5.opExtrude","SWEPT_FACE",FACE,{"disambiguationData":[OSD([sQuery(id+"F4.wireOp",EDGE,"E30")])]}),makeQuery(id+"F8.opExtrude","SWEPT_FACE",FACE,{"disambiguationData":[OSD([sQuery(id+"F7.wireOp",EDGE,"E67")])]})]});
            fillet(context, id + "F14", {"entities" : qUnion([Q0, Q1, Q2, Q3, Q4, Q5]), "radius" : 3 * mm, "tangentPropagation" : true, "allowEdgeOverflow" : false});
        }
        {
            var Q0;
            Q0=makeQuery(id+"F1.opExtrude","CAP_EDGE",EDGE,{"disambiguationData":[OSD([sQuery(id+"F0.wireOp",EDGE,"E1.bottom")])],"isStart":false});
            fillet(context, id + "F15", {"entities" : qUnion([Q0]), "radius" : 2 * mm, "tangentPropagation" : true, "allowEdgeOverflow" : false});
        }
        {
            var Q0;
            {var subQ0=sQuery(id+"F0.wireOp",EDGE,"E22.filletArc");var subQ1=sQuery(id+"F0.wireOp",EDGE,"E7");var subQ2=sQuery(id+"F0.wireOp",EDGE,"E6");var subQ3=sQuery(id+"F0.wireOp",EDGE,"E5");var subQ4=sQuery(id+"F0.wireOp",EDGE,"E4");var subQ5=sQuery(id+"F0.wireOp",EDGE,"E1.bottom");var subQ6=sQuery(id+"F0.wireOp",EDGE,"E21.filletArc");var subQ7=sQuery(id+"F0.wireOp",EDGE,"E1.top");var subQ8=sQuery(id+"F0.wireOp",EDGE,"E1.left");var subQ9=sQuery(id+"F0.wireOp",EDGE,"E1.right");var subQ10=sQuery(id+"F0.wireOp",EDGE,"E23.filletArc");var subQ11=sQuery(id+"F0.wireOp",EDGE,"E24.filletArc");Q0=makeQuery(id+"F2.boolean.opBoolean","SPLIT",FACE,{"disambiguationData":[TD([makeQuery(id+"F1.opExtrude","SWEPT_FACE",FACE,{"disambiguationData":[OSD([subQ5])]})])],"derivedFrom":makeQuery(id+"F1.opExtrude","CAP_FACE",FACE,{"disambiguationData":[OSD([subQ5,subQ7,subQ8,subQ9,subQ4,subQ3,subQ2,subQ1,subQ6,subQ0,subQ10,subQ11])],"isStart":true})});}
            var sketch = newSketch(context, id + "F16", { "sketchPlane" : qUnion([Q0])});
            skArc(sketch, "E79.0", {"start": v(-70, 90) * mm, "mid": v(-77.07, 87.07) * mm, "end": v(-80, 80) * mm});
            skLineSegment(sketch, "E79.1", {"start": v(-80, -80) * mm, "end": v(-80, 80) * mm});
            skArc(sketch, "E79.2", {"start": v(-80, -80) * mm, "mid": v(-77.07, -87.07) * mm, "end": v(-70, -90) * mm});
            skLineSegment(sketch, "E79.3", {"start": v(-70, -90) * mm, "end": v(70, -90) * mm});
            skArc(sketch, "E79.4", {"start": v(70, -90) * mm, "mid": v(77.07, -87.07) * mm, "end": v(80, -80) * mm});
            skLineSegment(sketch, "E79.5", {"start": v(80, -80) * mm, "end": v(80, 80) * mm});
            skArc(sketch, "E79.6", {"start": v(80, 80) * mm, "mid": v(77.07, 87.07) * mm, "end": v(70, 90) * mm});
            skLineSegment(sketch, "E79.7", {"start": v(-70, 90) * mm, "end": v(70, 90) * mm});
            skArc(sketch, "E79.8", {"start": v(56.15, 48.18) * mm, "mid": v(0, 67.5) * mm, "end": v(-56.15, 48.18) * mm});
            skCircle(sketch, "E79.9", {"center": v(-60, 67.5) * mm, "radius": 4 * mm});
            skArc(sketch, "E79.10", {"start": v(-56.15, 48.18) * mm, "mid": v(-58.99, 44.68) * mm, "end": v(-60, 40.3) * mm});
            skLineSegment(sketch, "E79.11", {"start": v(-60, 40.3) * mm, "end": v(-60, -40.3) * mm});
            skArc(sketch, "E79.12", {"start": v(-60, -40.3) * mm, "mid": v(-58.99, -44.68) * mm, "end": v(-56.15, -48.18) * mm});
            skCircle(sketch, "E79.13", {"center": v(-60, -67.5) * mm, "radius": 4 * mm});
            skArc(sketch, "E79.14", {"start": v(-56.15, -48.18) * mm, "mid": v(0, -67.5) * mm, "end": v(56.15, -48.18) * mm});
            skCircle(sketch, "E79.15", {"center": v(60, -67.5) * mm, "radius": 4 * mm});
            skArc(sketch, "E79.16", {"start": v(56.15, -48.18) * mm, "mid": v(58.99, -44.68) * mm, "end": v(60, -40.3) * mm});
            skLineSegment(sketch, "E79.17", {"start": v(60, 40.3) * mm, "end": v(60, -40.3) * mm});
            skCircle(sketch, "E79.18", {"center": v(60, 67.5) * mm, "radius": 4 * mm});
            skArc(sketch, "E79.19", {"start": v(60, 40.3) * mm, "mid": v(58.99, 44.68) * mm, "end": v(56.15, 48.18) * mm});
            skLineSegment(sketch, "E80", {"start": v(0, 23.75) * mm, "end": v(0, 120) * mm, "construction": true});
            skCircle(sketch, "E81", {"center": v(0, 120) * mm, "radius": 6 * mm});
            skLineSegment(sketch, "E82", {"start": v(-15, 120) * mm, "end": v(-15, 108) * mm});
            skLineSegment(sketch, "E83", {"start": v(-15, 108) * mm, "end": v(-33, 90) * mm});
            skLineSegment(sketch, "E84", {"start": v(15, 120) * mm, "end": v(15, 108) * mm});
            skLineSegment(sketch, "E85", {"start": v(15, 108) * mm, "end": v(33, 90) * mm});
            skArc(sketch, "E86", {"start": v(15, 120) * mm, "mid": v(0, 135) * mm, "end": v(-15, 120) * mm});
            skLineSegment(sketch, "E87", {"start": v(92.67, 0) * mm, "end": v(-87.04, 0) * mm, "construction": true});
            skPoint(sketch, "E87.startSnap0", {"position": v(80, 0) * mm});
            skPoint(sketch, "E87.endSnap0", {"position": v(-80, 0) * mm});
            skArc(sketch, "E88.MirrorCS", {"start": v(-15, 120) * mm, "mid": v(0, 135) * mm, "end": v(15, 120) * mm});
            skLineSegment(sketch, "E89.MirrorCS", {"start": v(15, -108) * mm, "end": v(33, -90) * mm});
            skLineSegment(sketch, "E90.MirrorCS", {"start": v(-15, -108) * mm, "end": v(-33, -90) * mm});
            skLineSegment(sketch, "E91.MirrorCS", {"start": v(-15, -120) * mm, "end": v(-15, -108) * mm});
            skCircle(sketch, "E92.MirrorC", {"center": v(0, -120) * mm, "radius": 6 * mm});
            skLineSegment(sketch, "E93.MirrorCS", {"start": v(15, -120) * mm, "end": v(15, -108) * mm});
            skArc(sketch, "E94.MirrorCS", {"start": v(-15, -120) * mm, "mid": v(0, -135) * mm, "end": v(15, -120) * mm});
            skArc(sketch, "E95.MirrorCS", {"start": v(15, -120) * mm, "mid": v(0, -135) * mm, "end": v(-15, -120) * mm});
            skLineSegment(sketch, "E96.MirrorCS", {"start": v(0, -23.75) * mm, "end": v(0, -120) * mm, "construction": true});
            skSolve(sketch);
        }
        {
            var Q0;
            Q0 = qSketchRegion(id + "F16", true);
            var Q1;
            Q1=makeQuery(id+"F2.opExtrude","CAP_FACE",FACE,{"disambiguationData":[OSD([sQuery(id+"F0.wireOp",EDGE,"E12"),sQuery(id+"F0.wireOp",EDGE,"E13"),sQuery(id+"F0.wireOp",EDGE,"E14"),sQuery(id+"F0.wireOp",EDGE,"E15"),sQuery(id+"F0.wireOp",EDGE,"E17.filletArc"),sQuery(id+"F0.wireOp",EDGE,"E18.filletArc"),sQuery(id+"F0.wireOp",EDGE,"E19.filletArc"),sQuery(id+"F0.wireOp",EDGE,"E20.filletArc"),sQuery(id+"F0.wireOp",EDGE,"E25.0"),sQuery(id+"F0.wireOp",EDGE,"E25.1"),sQuery(id+"F0.wireOp",EDGE,"E25.2"),sQuery(id+"F0.wireOp",EDGE,"E25.3"),sQuery(id+"F0.wireOp",EDGE,"E25.4"),sQuery(id+"F0.wireOp",EDGE,"E25.5"),sQuery(id+"F0.wireOp",EDGE,"E25.6"),sQuery(id+"F0.wireOp",EDGE,"E25.7")])],"isStart":false});
            extrude(context, id + "F17", {"entities" : qUnion([Q0]), "endBound" : BoundingType.UP_TO_SURFACE, "endBoundEntityFace" : qUnion([Q1]), "depth" : 25 * mm});
        }
    });
